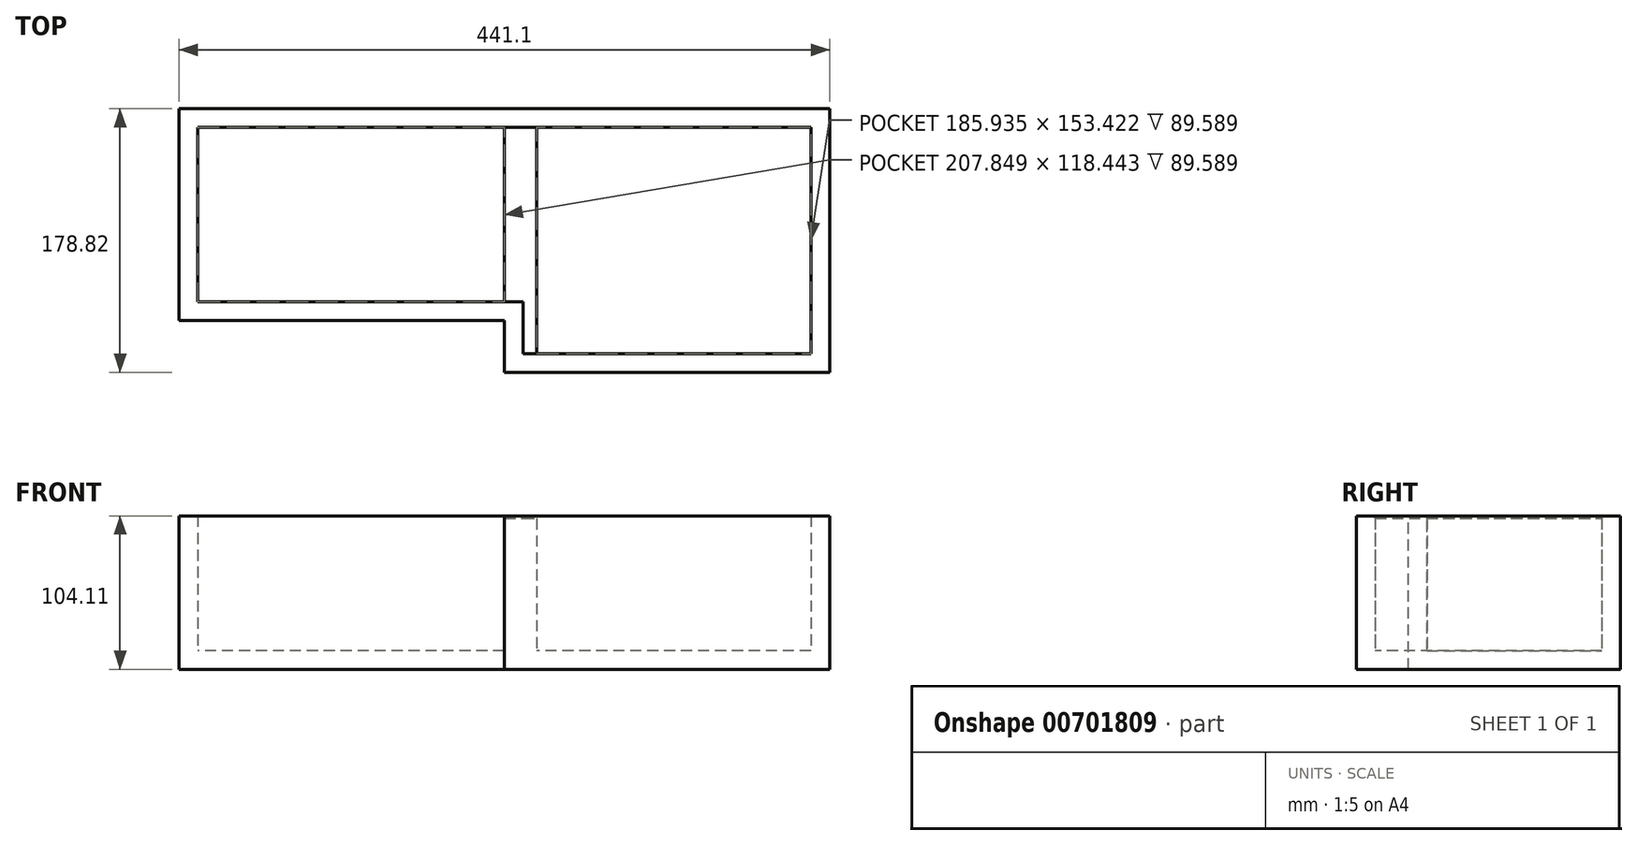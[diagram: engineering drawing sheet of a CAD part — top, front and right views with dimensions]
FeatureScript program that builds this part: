
annotation { "Feature Type Name" : "Feature", "Feature Type Description" : "" }
export const myFeature = defineFeature(function(context is Context, id is Id, definition is map)
    precondition{}
    {
        {
            var Q0;
            Q0=qCreatedBy(makeId("Top.planeOp"),FACE);
            var sketch = newSketch(context, id + "F0", { "sketchPlane" : qUnion([Q0])});
            skLineSegment(sketch, "E0.bottom", {"start": v(220.55, -89.41) * mm, "end": v(-220.55, -89.41) * mm});
            skLineSegment(sketch, "E0.top", {"start": v(220.55, 89.41) * mm, "end": v(-220.55, 89.41) * mm});
            skLineSegment(sketch, "E0.left", {"start": v(220.55, -89.41) * mm, "end": v(220.55, 89.41) * mm});
            skLineSegment(sketch, "E0.right", {"start": v(-220.55, -89.41) * mm, "end": v(-220.55, 89.41) * mm});
            skPoint(sketch, "E0.middle", {"position": v(0, 0) * mm});
            skSolve(sketch);
        }
        {
            var Q0;
            Q0=makeQuery(id+"F0.imprint","IMPRINT",FACE,{"disambiguationData":[TD([[makeQuery(id+"F0.imprint","IMPRINT",EDGE,{"derivedFrom":sQuery(id+"F0.wireOp",EDGE,"E0.bottom")}),-1.0]])]});
            extrude(context, id + "F1", {"entities" : qUnion([Q0]), "depth" : 104.1 * mm, "offsetDistance" : 25.4 * mm});
        }
        {
            var Q0;
            Q0=makeQuery(id+"F1.opExtrude","CAP_FACE",FACE,{"disambiguationData":[OSD([sQuery(id+"F0.wireOp",EDGE,"E0.bottom"),sQuery(id+"F0.wireOp",EDGE,"E0.top"),sQuery(id+"F0.wireOp",EDGE,"E0.left"),sQuery(id+"F0.wireOp",EDGE,"E0.right")])],"isStart":false});
            var sketch = newSketch(context, id + "F2", { "sketchPlane" : qUnion([Q0])});
            skLineSegment(sketch, "E1.bottom", {"start": v(-220.55, -89.41) * mm, "end": v(0, -89.41) * mm});
            skLineSegment(sketch, "E1.top", {"start": v(-220.55, -54.43) * mm, "end": v(0, -54.43) * mm});
            skLineSegment(sketch, "E1.left", {"start": v(-220.55, -89.41) * mm, "end": v(-220.55, -54.43) * mm});
            skLineSegment(sketch, "E1.right", {"start": v(0, -89.41) * mm, "end": v(0, -54.43) * mm});
            skSolve(sketch);
        }
        {
            var Q0;
            Q0 = qSketchRegion(id + "F2", true);
            extrude(context, id + "F3", {"entities" : qUnion([Q0]), "operationType" : NewBodyOperationType.REMOVE, "oppositeDirection" : true, "depth" : 137.2 * mm, "offsetDistance" : 25.4 * mm});
        }
        {
            var Q0;
            Q0=makeQuery(id+"F1.opExtrude","CAP_FACE",FACE,{"disambiguationData":[OSD([sQuery(id+"F0.wireOp",EDGE,"E0.bottom"),sQuery(id+"F0.wireOp",EDGE,"E0.top"),sQuery(id+"F0.wireOp",EDGE,"E0.left"),sQuery(id+"F0.wireOp",EDGE,"E0.right")])],"isStart":false});
            shell(context, id + "F4", {"entities" : qUnion([Q0]), "thickness" : 12.7 * mm});
        }
        {
            var Q0;
            Q0=makeQuery(id+"F1.opExtrude","CAP_FACE",FACE,{"disambiguationData":[OSD([sQuery(id+"F0.wireOp",EDGE,"E0.bottom"),sQuery(id+"F0.wireOp",EDGE,"E0.top"),sQuery(id+"F0.wireOp",EDGE,"E0.left"),sQuery(id+"F0.wireOp",EDGE,"E0.right")])],"isStart":true});
            var sketch = newSketch(context, id + "F5", { "sketchPlane" : qUnion([Q0])});
            skLineSegment(sketch, "E2", {"start": v(0, 89.41) * mm, "end": v(0, -89.41) * mm});
            skLineSegment(sketch, "E3", {"start": v(21.91, 89.41) * mm, "end": v(21.91, -89.41) * mm});
            skLineSegment(sketch, "E4", {"start": v(0, 89.41) * mm, "end": v(21.91, 89.41) * mm});
            skLineSegment(sketch, "E5", {"start": v(0, -89.41) * mm, "end": v(21.91, -89.41) * mm});
            skSolve(sketch);
        }
        {
            var Q0;
            Q0 = qSketchRegion(id + "F5", true);
            extrude(context, id + "F6", {"entities" : qUnion([Q0]), "operationType" : NewBodyOperationType.ADD, "oppositeDirection" : true, "depth" : 102.3 * mm, "offsetDistance" : 25.4 * mm});
        }
    });
